# Revit family: Kubus M LED 1-s Sentr (venstre_veggmontasje)
name_source: partatom
category: Lighting Fixtures
revit_build: Autodesk Revit 2013 (Build: 20130531_2115(x64)
units: mm (PartAtom-declared; Revit-internal decimal feet)

## types (3) — shared parameters
Apparent Load = 17 VA
Body Material and Colour = Default
Color Filter = 16777215
Dimming Lamp Color Temperature Shift = <None>
Emit Shape Visible in Rendering = No
Lamp = 1
Number of Poles = 1
Photometric Web File = 20x42A12.ies
Tilt Angle = 90.00°
Voltage = 230 V
Wattage Comments = 17 W
Width = 70 mm

## per-type parameters (varying)
| type | 23m | 35m | 60m | Emit from Rectangle Length | Emit from Rectangle Width | Height | Height 1 | Length | Length 1 |
| 23m | Yes | No | No | 255 mm  [stored 0.836614 ft] | 140 mm  [stored 0.459318 ft] | 140 mm  [stored 0.459318 ft] | 110 mm | 255 mm  [stored 0.836614 ft] | 225 mm |
| 35m | No | Yes | No | 376 mm | 200 mm | 200 mm | 170 mm  [stored 0.557743 ft] | 376 mm | 346 mm  [stored 1.13517 ft] |
| 60m | No | No | Yes | 605 mm  [stored 1.98491 ft] | 315 mm | 315 mm | 285 mm | 605 mm  [stored 1.98491 ft] | 575 mm |

note: [stored X ft] marks values corroborated as IEEE doubles in the binary element streams (Revit-internal decimal feet)

## geometry (parser evidence)
native form markers: Blend x2, Sweep x8
no freeform markers — native parametric forms only
